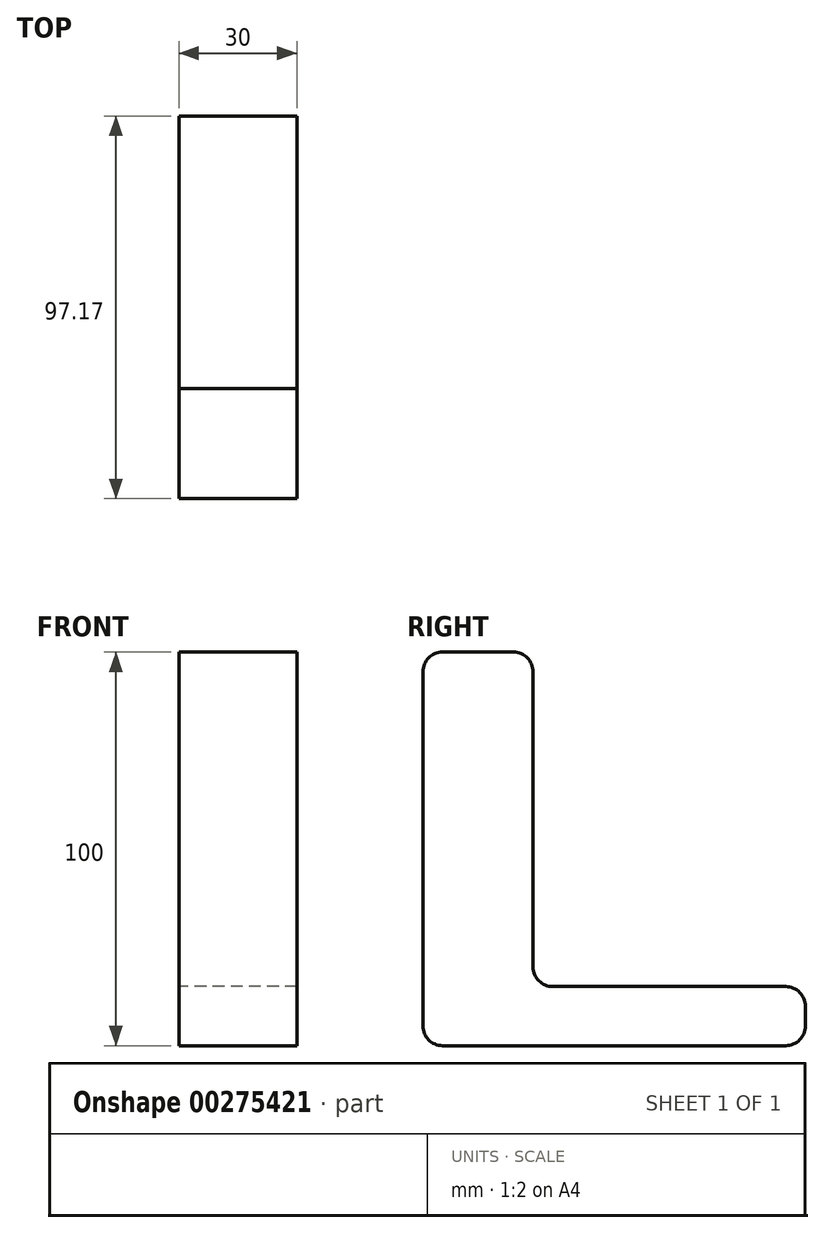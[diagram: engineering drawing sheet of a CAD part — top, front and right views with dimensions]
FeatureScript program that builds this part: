
annotation { "Feature Type Name" : "Feature", "Feature Type Description" : "" }
export const myFeature = defineFeature(function(context is Context, id is Id, definition is map)
    precondition{}
    {
        {
            var Q0;
            Q0=qCreatedBy(makeId("Right.planeOp"),FACE);
            var sketch = newSketch(context, id + "F0", { "sketchPlane" : qUnion([Q0])});
            skLineSegment(sketch, "E0", {"start": v(-48.75, 39.78) * mm, "end": v(-30.75, 39.78) * mm});
            skLineSegment(sketch, "E1", {"start": v(-25.75, 34.78) * mm, "end": v(-25.75, -40.22) * mm});
            skLineSegment(sketch, "E2", {"start": v(-20.75, -45.22) * mm, "end": v(38.42, -45.22) * mm});
            skLineSegment(sketch, "E3", {"start": v(43.42, -50.22) * mm, "end": v(43.42, -55.22) * mm});
            skLineSegment(sketch, "E4", {"start": v(38.42, -60.22) * mm, "end": v(-48.75, -60.22) * mm});
            skLineSegment(sketch, "E5", {"start": v(-53.75, -55.22) * mm, "end": v(-53.75, 34.78) * mm});
            skPoint(sketch, "E6.visualSharp", {"position": v(-53.75, 39.78) * mm});
            skArc(sketch, "E6.filletArc", {"start": v(-48.75, 39.78) * mm, "mid": v(-52.28, 38.32) * mm, "end": v(-53.75, 34.78) * mm});
            skPoint(sketch, "E7.visualSharp", {"position": v(-25.75, 39.78) * mm});
            skArc(sketch, "E7.filletArc", {"start": v(-25.75, 34.78) * mm, "mid": v(-27.21, 38.32) * mm, "end": v(-30.75, 39.78) * mm});
            skPoint(sketch, "E8.visualSharp", {"position": v(-53.75, -60.22) * mm});
            skArc(sketch, "E8.filletArc", {"start": v(-53.75, -55.22) * mm, "mid": v(-52.28, -58.75) * mm, "end": v(-48.75, -60.22) * mm});
            skPoint(sketch, "E9.visualSharp", {"position": v(-25.75, -45.22) * mm});
            skArc(sketch, "E9.filletArc", {"start": v(-25.75, -40.22) * mm, "mid": v(-24.28, -43.75) * mm, "end": v(-20.75, -45.22) * mm});
            skPoint(sketch, "E10.visualSharp", {"position": v(43.42, -45.22) * mm});
            skArc(sketch, "E10.filletArc", {"start": v(43.42, -50.22) * mm, "mid": v(41.95, -46.68) * mm, "end": v(38.42, -45.22) * mm});
            skPoint(sketch, "E11.visualSharp", {"position": v(43.42, -60.22) * mm});
            skArc(sketch, "E11.filletArc", {"start": v(38.42, -60.22) * mm, "mid": v(41.95, -58.75) * mm, "end": v(43.42, -55.22) * mm});
            skSolve(sketch);
        }
        {
            var Q0;
            Q0=makeQuery(id+"F0.imprint","IMPRINT",FACE,{"disambiguationData":[TD([[makeQuery(id+"F0.imprint","IMPRINT",EDGE,{"derivedFrom":sQuery(id+"F0.wireOp",EDGE,"E0")}),-1.0]])]});
            extrude(context, id + "F1", {"entities" : qUnion([Q0]), "depth" : 30 * mm, "offsetDistance" : 25 * mm});
        }
    });
